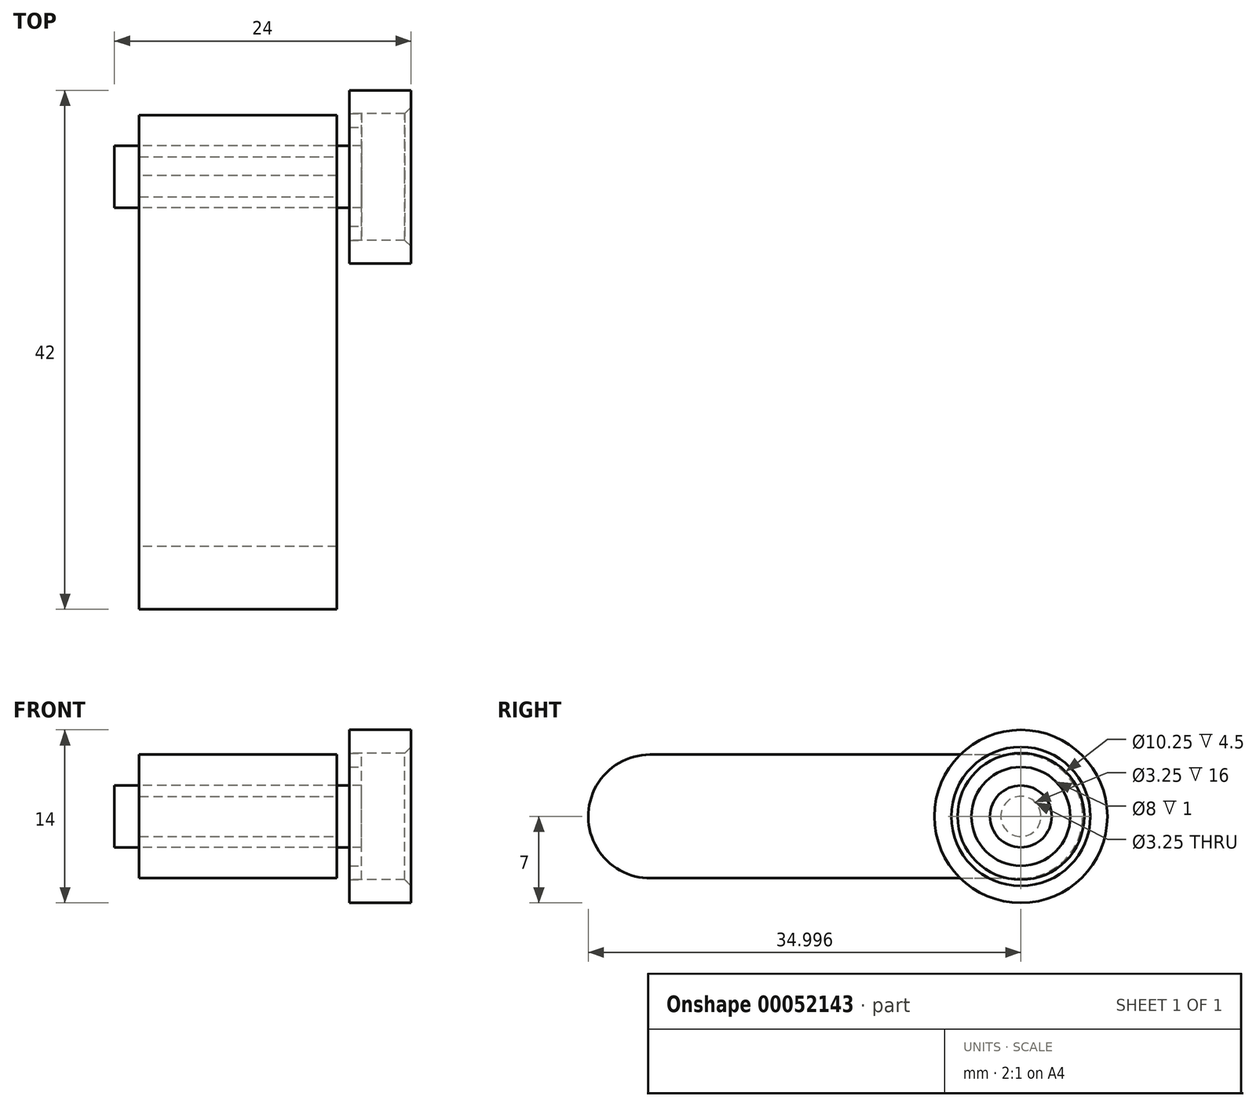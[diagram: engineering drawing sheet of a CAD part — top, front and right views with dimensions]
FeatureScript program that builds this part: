
annotation { "Feature Type Name" : "Feature", "Feature Type Description" : "" }
export const myFeature = defineFeature(function(context is Context, id is Id, definition is map)
    precondition{}
    {
        {
            var Q0;
            Q0=qCreatedBy(makeId("Right.planeOp"),FACE);
            var sketch = newSketch(context, id + "F0", { "sketchPlane" : qUnion([Q0])});
            skLineSegment(sketch, "E0.rect.bottom", {"start": v(-14.96, -5) * mm, "end": v(15.04, -5) * mm});
            skLineSegment(sketch, "E0.rect.top", {"start": v(-15.04, 5) * mm, "end": v(14.96, 5) * mm});
            skPoint(sketch, "E0.rect.middle", {"position": v(0, 0) * mm});
            skArc(sketch, "E1", {"start": v(14.96, 5) * mm, "mid": v(19.96, 0.04) * mm, "end": v(15.04, -5) * mm});
            skArc(sketch, "E2", {"start": v(-15.04, 5) * mm, "mid": v(-20.04, -0.04) * mm, "end": v(-14.96, -5) * mm});
            skSolve(sketch);
        }
        {
            var Q0;
            Q0 = qSketchRegion(id + "F0", true);
            extrude(context, id + "F1", {"entities" : qUnion([Q0]), "depth" : 8 * mm, "hasSecondDirection" : true, "secondDirectionOppositeDirection" : true, "secondDirectionDepth" : 8 * mm});
        }
        {
            var Q0;
            Q0=qCreatedBy(makeId("Right.planeOp"),FACE);
            var sketch = newSketch(context, id + "F2", { "sketchPlane" : qUnion([Q0])});
            skCircle(sketch, "E3", {"center": v(14.96, 0) * mm, "radius": 2.5 * mm});
            skSolve(sketch);
        }
        {
            var Q0;
            Q0 = qSketchRegion(id + "F2", true);
            extrude(context, id + "F3", {"entities" : qUnion([Q0]), "depth" : 10 * mm, "hasSecondDirection" : true, "secondDirectionOppositeDirection" : true, "secondDirectionDepth" : 10 * mm});
        }
        {
            var Q0;
            Q0=qCreatedBy(makeId("Right.planeOp"),FACE);
            var sketch = newSketch(context, id + "F4", { "sketchPlane" : qUnion([Q0])});
            skCircle(sketch, "E4", {"center": v(14.96, 0) * mm, "radius": 1.63 * mm});
            skSolve(sketch);
        }
        {
            var Q0;
            Q0 = qSketchRegion(id + "F4", true);
            extrude(context, id + "F5", {"entities" : qUnion([Q0]), "operationType" : NewBodyOperationType.REMOVE, "endBound" : BoundingType.UP_TO_NEXT, "oppositeDirection" : true, "depth" : 25 * mm, "hasSecondDirection" : true, "secondDirectionBound" : SecondDirectionBoundingType.UP_TO_NEXT, "secondDirectionOppositeDirection" : false, "secondDirectionDepth" : 11 * mm});
        }
        {
            var Q0;
            Q0=makeQuery(id+"F3.opExtrude","CAP_FACE",FACE,{"disambiguationData":[OSD([sQuery(id+"F2.wireOp",EDGE,"E3")])],"isStart":false});
            var sketch = newSketch(context, id + "F6", { "sketchPlane" : qUnion([Q0])});
            skCircle(sketch, "E5", {"center": v(14.96, 0) * mm, "radius": 4 * mm});
            skCircle(sketch, "E6", {"center": v(14.96, 0) * mm, "radius": 5.12 * mm});
            skSolve(sketch);
        }
        {
            var Q0;
            Q0=makeQuery(id+"F6.imprint","IMPRINT",FACE,{"disambiguationData":[TD([[makeQuery(id+"F6.imprint","IMPRINT",EDGE,{"derivedFrom":sQuery(id+"F6.wireOp",EDGE,"E5")}),-1.0]])]});
            extrude(context, id + "F7", {"entities" : qUnion([Q0]), "oppositeDirection" : true, "depth" : 1 * mm});
        }
        {
            var Q0;
            Q0=makeQuery(id+"F7.opExtrude","CAP_FACE",FACE,{"disambiguationData":[OSD([sQuery(id+"F6.wireOp",EDGE,"E5"),sQuery(id+"F6.wireOp",EDGE,"E6")])],"isStart":true});
            var sketch = newSketch(context, id + "F8", { "sketchPlane" : qUnion([Q0])});
            skCircle(sketch, "E7", {"center": v(14.96, 0) * mm, "radius": 5.12 * mm});
            skCircle(sketch, "E8", {"center": v(14.96, 0) * mm, "radius": 7 * mm});
            skSolve(sketch);
        }
        {
            var Q0;
            Q0=makeQuery(id+"F8.imprint","IMPRINT",FACE,{"disambiguationData":[TD([[makeQuery(id+"F8.imprint","IMPRINT",EDGE,{"derivedFrom":sQuery(id+"F8.wireOp",EDGE,"E7")}),-1.0]])]});
            extrude(context, id + "F9", {"entities" : qUnion([Q0]), "depth" : 4 * mm, "hasSecondDirection" : true, "secondDirectionOppositeDirection" : true, "secondDirectionDepth" : 1 * mm});
        }
        {
            var Q0;
            Q0=makeQuery(id+"F9.opExtrude","CAP_EDGE",EDGE,{"disambiguationData":[OSD([sQuery(id+"F8.wireOp",EDGE,"E7")])],"isStart":false});
            chamfer(context, id + "F10", {"entities" : qUnion([Q0]), "width" : 0.5 * mm, "tangentPropagation" : true});
        }
    });
